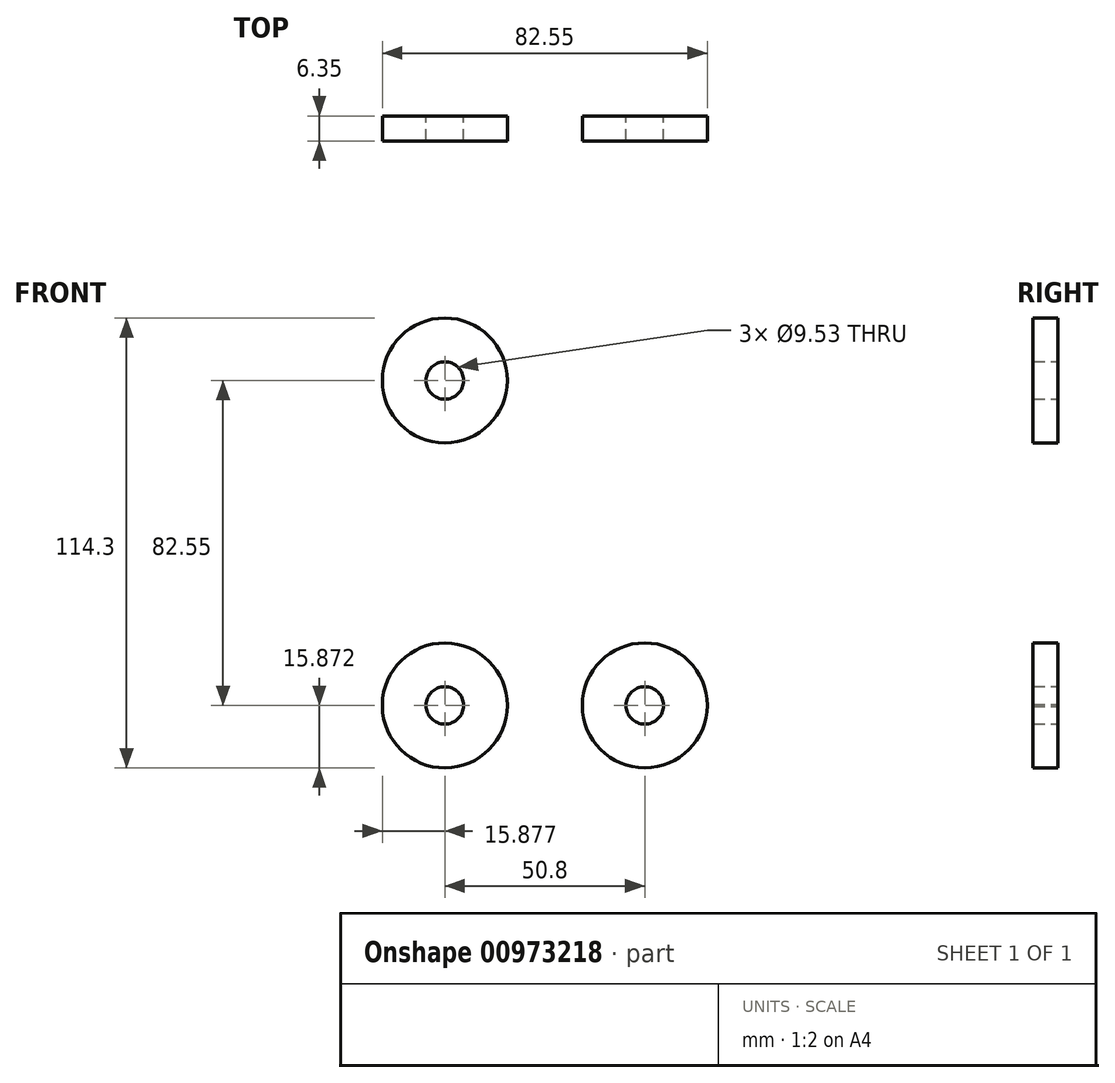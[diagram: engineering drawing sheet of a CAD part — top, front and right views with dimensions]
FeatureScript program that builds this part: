
annotation { "Feature Type Name" : "Feature", "Feature Type Description" : "" }
export const myFeature = defineFeature(function(context is Context, id is Id, definition is map)
    precondition{}
    {
        {
            var Q0;
            Q0=qCreatedBy(makeId("Front.planeOp"),FACE);
            var sketch = newSketch(context, id + "F0", { "sketchPlane" : qUnion([Q0])});
            skCircle(sketch, "E0", {"center": v(-188.37, 44.44) * mm, "radius": 4.76 * mm});
            skCircle(sketch, "E1", {"center": v(-188.37, -38.1) * mm, "radius": 4.76 * mm});
            skCircle(sketch, "E2", {"center": v(-137.57, -38.1) * mm, "radius": 4.76 * mm});
            skCircle(sketch, "E3", {"center": v(-188.37, 44.44) * mm, "radius": 15.88 * mm});
            skCircle(sketch, "E4", {"center": v(-188.37, -38.1) * mm, "radius": 15.88 * mm});
            skCircle(sketch, "E5", {"center": v(-137.57, -38.1) * mm, "radius": 15.88 * mm});
            skLineSegment(sketch, "E6", {"start": v(-204.25, 44.23) * mm, "end": v(-204.25, -38.32) * mm});
            skLineSegment(sketch, "E7", {"start": v(-188.37, -53.98) * mm, "end": v(-137.57, -53.98) * mm});
            skLineSegment(sketch, "E8", {"start": v(-121.7, -38.1) * mm, "end": v(-121.7, -6.36) * mm});
            skArc(sketch, "E9", {"start": v(-121.7, -6.36) * mm, "mid": v(-141.23, 40.79) * mm, "end": v(-188.37, 60.32) * mm});
            skCircle(sketch, "E10", {"center": v(-162.97, 3.17) * mm, "radius": 6.35 * mm});
            skSolve(sketch);
        }
        {
            var Q0;
            {var subQ5=sQuery(id+"F0.wireOp",EDGE,"E7");Q0=makeQuery(id+"F0.imprint","IMPRINT",FACE,{"disambiguationData":[TD([[makeQuery(id+"F0.imprint","IMPRINT",EDGE,{"derivedFrom":subQ5}),1.0]])]});}
            var Q1;
            Q1=makeQuery(id+"F0.imprint","IMPRINT",FACE,{"disambiguationData":[TD([[makeQuery(id+"F0.imprint","IMPRINT",EDGE,{"derivedFrom":sQuery(id+"F0.wireOp",EDGE,"E1")}),-1.0]])]});
            var Q2;
            Q2=makeQuery(id+"F0.imprint","IMPRINT",FACE,{"disambiguationData":[TD([[makeQuery(id+"F0.imprint","IMPRINT",EDGE,{"derivedFrom":sQuery(id+"F0.wireOp",EDGE,"E2")}),-1.0]])]});
            var Q3;
            Q3=makeQuery(id+"F0.imprint","IMPRINT",FACE,{"disambiguationData":[TD([[makeQuery(id+"F0.imprint","IMPRINT",EDGE,{"derivedFrom":sQuery(id+"F0.wireOp",EDGE,"E0")}),-1.0]])]});
            extrude(context, id + "F1", {"entities" : qUnion([Q0, Q1, Q2, Q3]), "depth" : 6.35 * mm, "offsetDistance" : 25.4 * mm});
        }
    });
